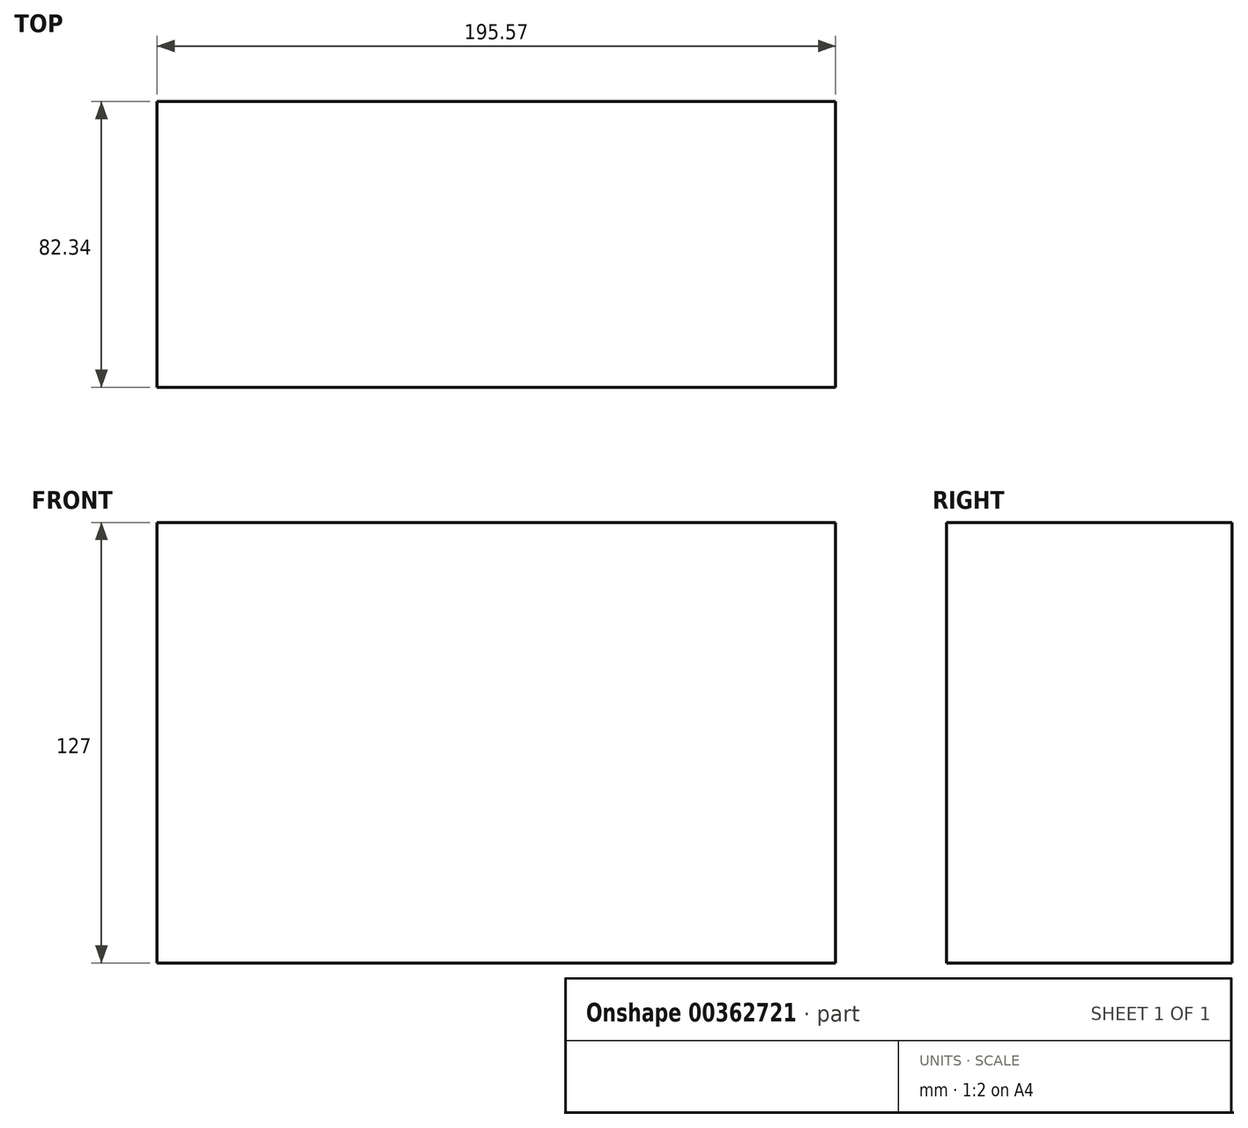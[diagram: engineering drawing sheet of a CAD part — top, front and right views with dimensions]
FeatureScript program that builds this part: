
annotation { "Feature Type Name" : "Feature", "Feature Type Description" : "" }
export const myFeature = defineFeature(function(context is Context, id is Id, definition is map)
    precondition{}
    {
        {
            var Q0;
            Q0=qCreatedBy(makeId("Top.planeOp"),FACE);
            var sketch = newSketch(context, id + "F0", { "sketchPlane" : qUnion([Q0])});
            skLineSegment(sketch, "E0.bottom", {"start": v(-55.26, 32.4) * mm, "end": v(140.3, 32.4) * mm});
            skLineSegment(sketch, "E0.top", {"start": v(-55.26, -49.93) * mm, "end": v(140.3, -49.93) * mm});
            skLineSegment(sketch, "E0.left", {"start": v(-55.26, 32.4) * mm, "end": v(-55.26, -49.93) * mm});
            skLineSegment(sketch, "E0.right", {"start": v(140.3, 32.4) * mm, "end": v(140.3, -49.93) * mm});
            skSolve(sketch);
        }
        {
            var Q0;
            Q0 = qSketchRegion(id + "F0", true);
            extrude(context, id + "F1", {"entities" : qUnion([Q0]), "depth" : 127 * mm});
        }
    });
